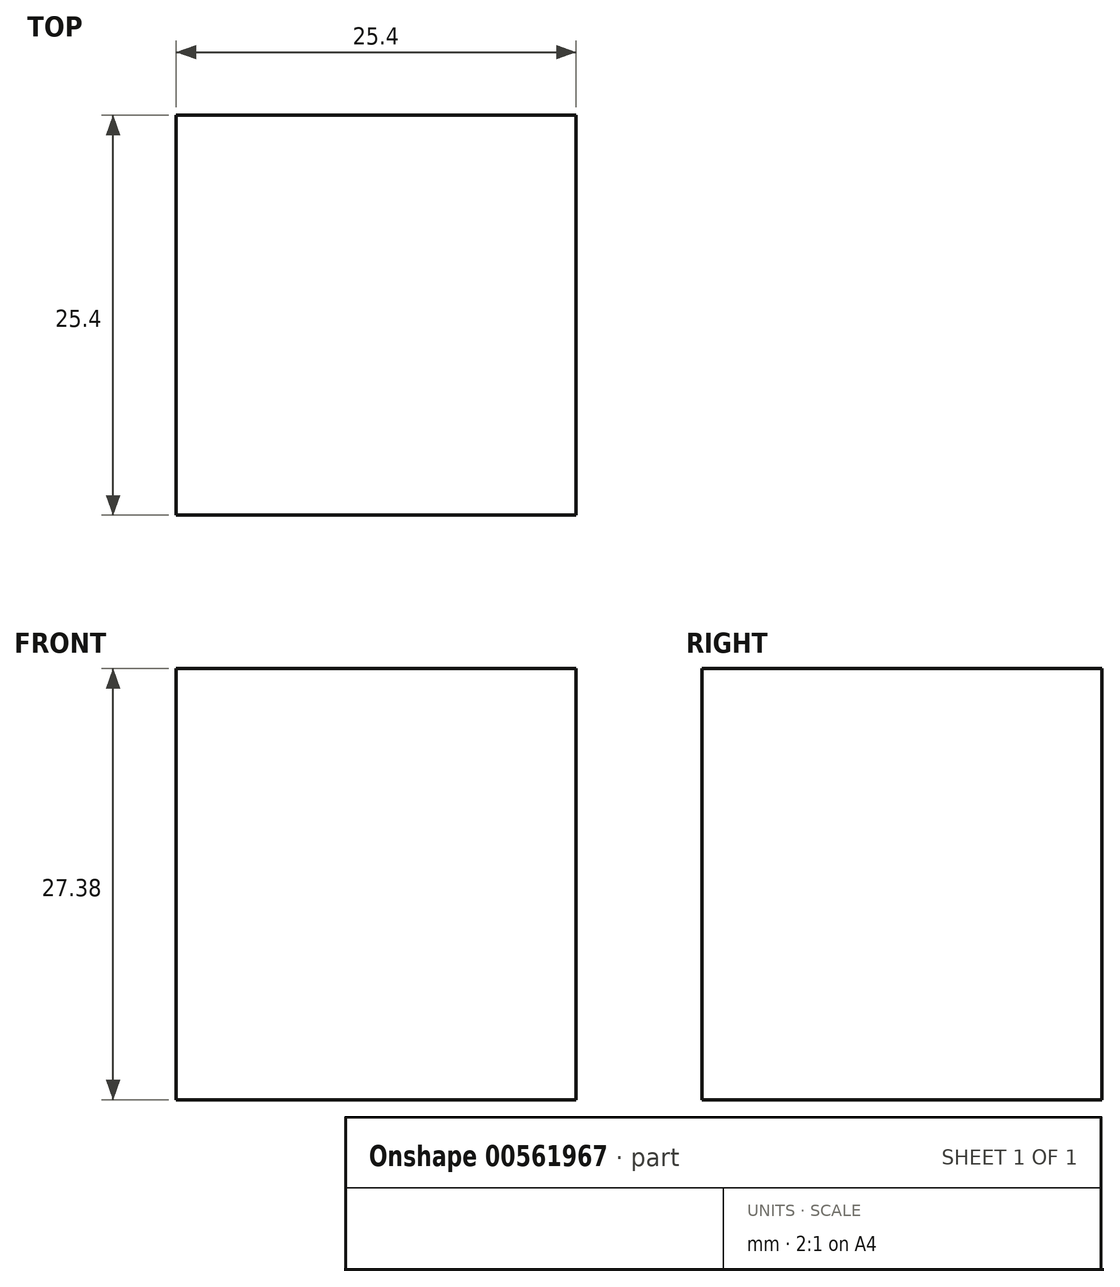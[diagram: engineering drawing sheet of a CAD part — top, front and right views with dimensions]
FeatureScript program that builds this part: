
annotation { "Feature Type Name" : "Feature", "Feature Type Description" : "" }
export const myFeature = defineFeature(function(context is Context, id is Id, definition is map)
    precondition{}
    {
        {
            var Q0;
            Q0=qCreatedBy(makeId("Front.planeOp"),FACE);
            var sketch = newSketch(context, id + "F0", { "sketchPlane" : qUnion([Q0])});
            skLineSegment(sketch, "E0.bottom", {"start": v(-53.16, 41) * mm, "end": v(-27.76, 41) * mm});
            skLineSegment(sketch, "E0.top", {"start": v(-53.16, 13.63) * mm, "end": v(-27.76, 13.63) * mm});
            skLineSegment(sketch, "E0.left", {"start": v(-53.16, 41) * mm, "end": v(-53.16, 13.63) * mm});
            skLineSegment(sketch, "E0.right", {"start": v(-27.76, 41) * mm, "end": v(-27.76, 13.63) * mm});
            skSolve(sketch);
        }
        {
            var Q0;
            Q0=makeQuery(id+"F0.imprint","IMPRINT",FACE,{"disambiguationData":[TD([[makeQuery(id+"F0.imprint","IMPRINT",EDGE,{"derivedFrom":sQuery(id+"F0.wireOp",EDGE,"E0.bottom")}),-1.0]])]});
            extrude(context, id + "F1", {"entities" : qUnion([Q0]), "depth" : 25.4 * mm, "offsetDistance" : 25.4 * mm});
        }
    });
